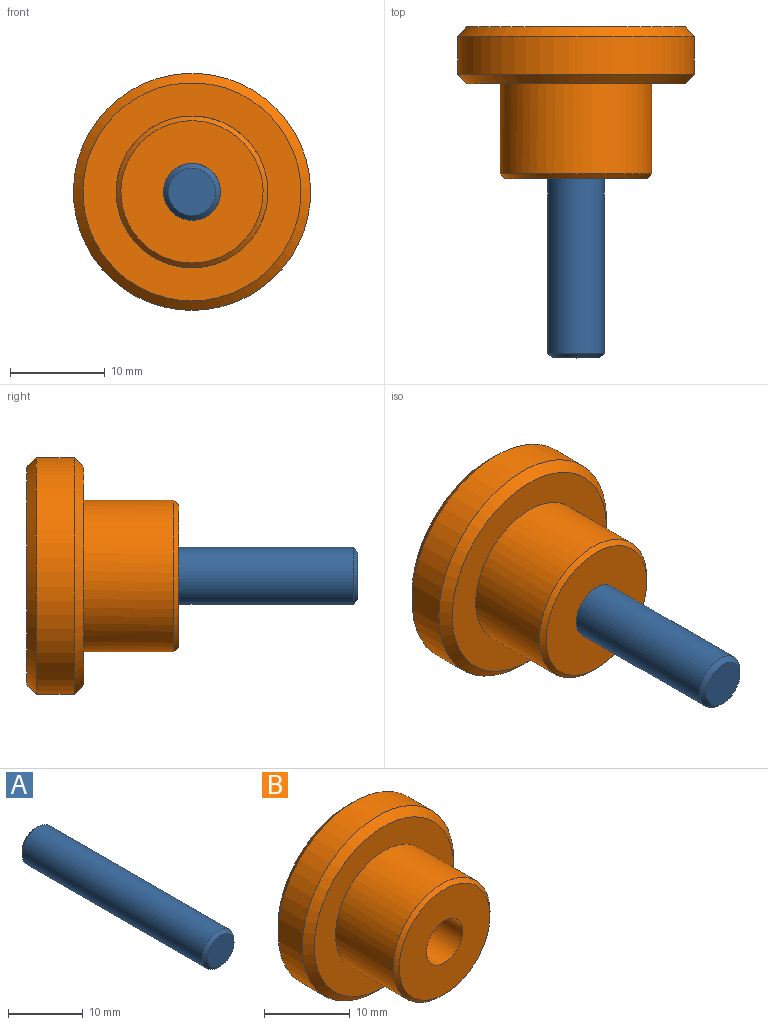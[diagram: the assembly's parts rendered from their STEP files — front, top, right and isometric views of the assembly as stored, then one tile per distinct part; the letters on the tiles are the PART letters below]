
ASSEMBLY  parts=2 mates=1
PART A: 5 faces, bbox 6x35x6 mm
  f0: cylinder r=3mm len=34mm, axis (0,1,0), area 640.9mm2, adj f3,f4
  f1: plane 5x5mm, normal (0,-1,0), area 19.6mm2, adj f3
  f2: plane 5x5mm, normal (0,1,0), area 19.6mm2, adj f4
  f3: cone r=2.5mm half-angle=45deg, axis (0,1,0), area 12.2mm2, adj f0,f1
  f4: cone r=3mm half-angle=45deg, axis (0,-1,0), area 12.2mm2, adj f0,f2
PART B: 9 faces, bbox 25x16x25 mm
  f0: cylinder r=12.5mm len=25mm, axis (0,1,0), area 314.2mm2, adj f6,f7
  f1: plane 23x23mm, normal (0,-1,0), area 214.4mm2, adj f3,f7
  f2: plane 23x23mm, normal (0,1,0), area 387.2mm2, adj f5,f6
  f3: cylinder r=8mm len=16mm, axis (0,1,0), area 477.5mm2, adj f1,f8
  f4: plane 15x15mm, normal (0,-1,0), area 148.4mm2, adj f5,f8
  f5: cylinder r=3mm len=16mm, axis (0,-1,0), area 301.6mm2, adj f2,f4
  f6: cone r=12.5mm half-angle=45deg, axis (0,-1,0), area 106.6mm2, adj f0,f2
  f7: cone r=11.5mm half-angle=45deg, axis (0,1,0), area 106.6mm2, adj f0,f1
  f8: cone r=7.5mm half-angle=45deg, axis (0,1,0), area 34.4mm2, adj f3,f4
PLACE A t=(0.2,-17.99,15.77)mm
PLACE B rot(axis=(0,-1,0),0deg) t=(0.2,-18.09,15.77)mm
MATE cylindrical A.f0 <-> B.f0  axis (0,1,0) through (0.2,-35.49,15.77)mm
